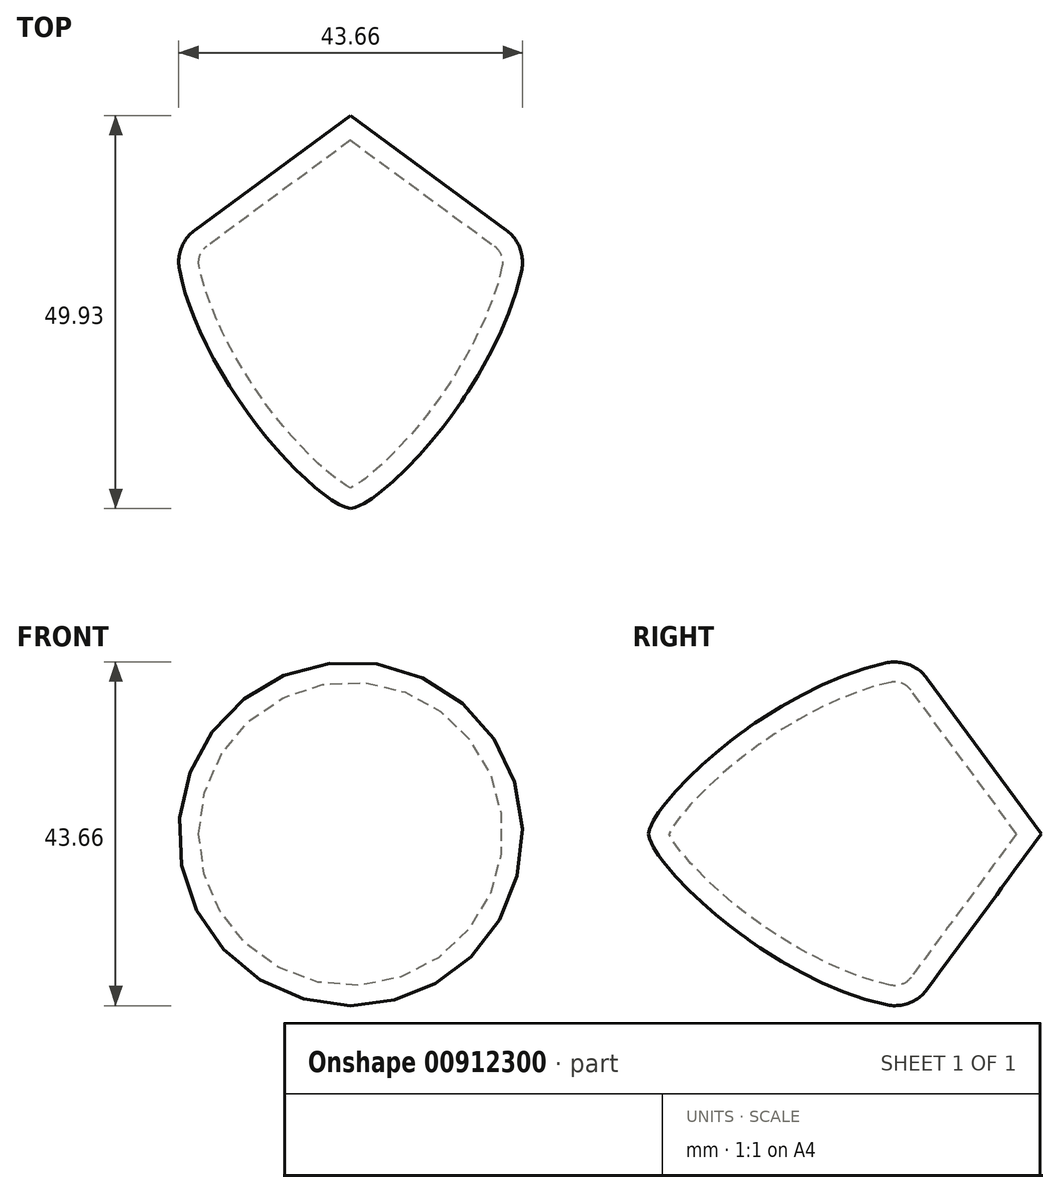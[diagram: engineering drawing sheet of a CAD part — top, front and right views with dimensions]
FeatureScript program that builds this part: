
annotation { "Feature Type Name" : "Feature", "Feature Type Description" : "" }
export const myFeature = defineFeature(function(context is Context, id is Id, definition is map)
    precondition{}
    {
        {
            var Q0;
            Q0=qCreatedBy(makeId("Top.planeOp"),FACE);
            var sketch = newSketch(context, id + "F0", { "sketchPlane" : qUnion([Q0])});
            skLineSegment(sketch, "E0", {"start": v(-22, 8.54) * mm, "end": v(0, 24.73) * mm});
            skLineSegment(sketch, "E1", {"start": v(0, 24.73) * mm, "end": v(0, -25.2) * mm});
            skFitSpline(sketch, "E2", {"points": [v(0, -25.2) * mm, v(-13.1, -13.02) * mm, v(-22, 8.54) * mm], "startDerivative": vector(-15.69, 1.65) * mm, "endDerivative": vector(2.11, 27.98) * mm});
            skSolve(sketch);
        }
        {
            var Q0;
            Q0=qCreatedBy(makeId("Right.planeOp"),FACE);
            var sketch = newSketch(context, id + "F1", { "sketchPlane" : qUnion([Q0])});
            skLineSegment(sketch, "E3", {"start": v(-10.34, 0) * mm, "end": v(24.7, 0) * mm});
            skSolve(sketch);
        }
        {
            var Q0;
            Q0=makeQuery(id+"F0.imprint","IMPRINT",FACE,{"disambiguationData":[TD([[makeQuery(id+"F0.imprint","IMPRINT",EDGE,{"derivedFrom":sQuery(id+"F0.wireOp",EDGE,"E0")}),-1.0]])]});
            var Q1;
            Q1=sQuery(id+"F1.wireOp",EDGE,"E3");
            revolve(context, id + "F2", {"surfaceOperationType" : NewSurfaceOperationType.NEW, "entities" : qUnion([Q0]), "axis" : qUnion([Q1]), "revolveType" : RevolveType.FULL});
        }
        {
            var Q0;
            Q0=makeQuery(id+"F2.opRevolve","SWEPT_EDGE",EDGE,{"disambiguationData":[OSD([sQuery(id+"F0.wireOp",EDGE,"E0"),sQuery(id+"F0.wireOp",EDGE,"E2")])]});
            fillet(context, id + "F3", {"entities" : qUnion([Q0]), "radius" : 5.08 * mm, "tangentPropagation" : true, "allowEdgeOverflow" : false});
        }
        {
            var Q0;
            Q0=makeQuery(id+"F2.opRevolve","SWEPT_FACE",FACE,{"disambiguationData":[OSD([sQuery(id+"F0.wireOp",EDGE,"E2")])]});
            var Q1;
            Q1=makeQuery(id+"F3.opFillet","BLEND_FACE",FACE,{"disambiguationData":[OSD([sQuery(id+"F0.wireOp",EDGE,"E0"),sQuery(id+"F0.wireOp",EDGE,"E2")])]});
            var Q2;
            Q2=makeQuery(id+"F2.opRevolve","SWEPT_FACE",FACE,{"disambiguationData":[OSD([sQuery(id+"F0.wireOp",EDGE,"E0")])]});
            var Q3;
            Q3=makeQuery(id+"F2.opRevolve","SWEPT_BODY",BODY,{"disambiguationData":[OSD([sQuery(id+"F0.wireOp",EDGE,"E0"),sQuery(id+"F0.wireOp",EDGE,"E1"),sQuery(id+"F0.wireOp",EDGE,"E2")])]});
            shell(context, id + "F4", {"isHollow" : true, "entities" : qUnion([Q0, Q1, Q2]), "parts" : qUnion([Q3]), "thickness" : 2.54 * mm});
        }
    });
